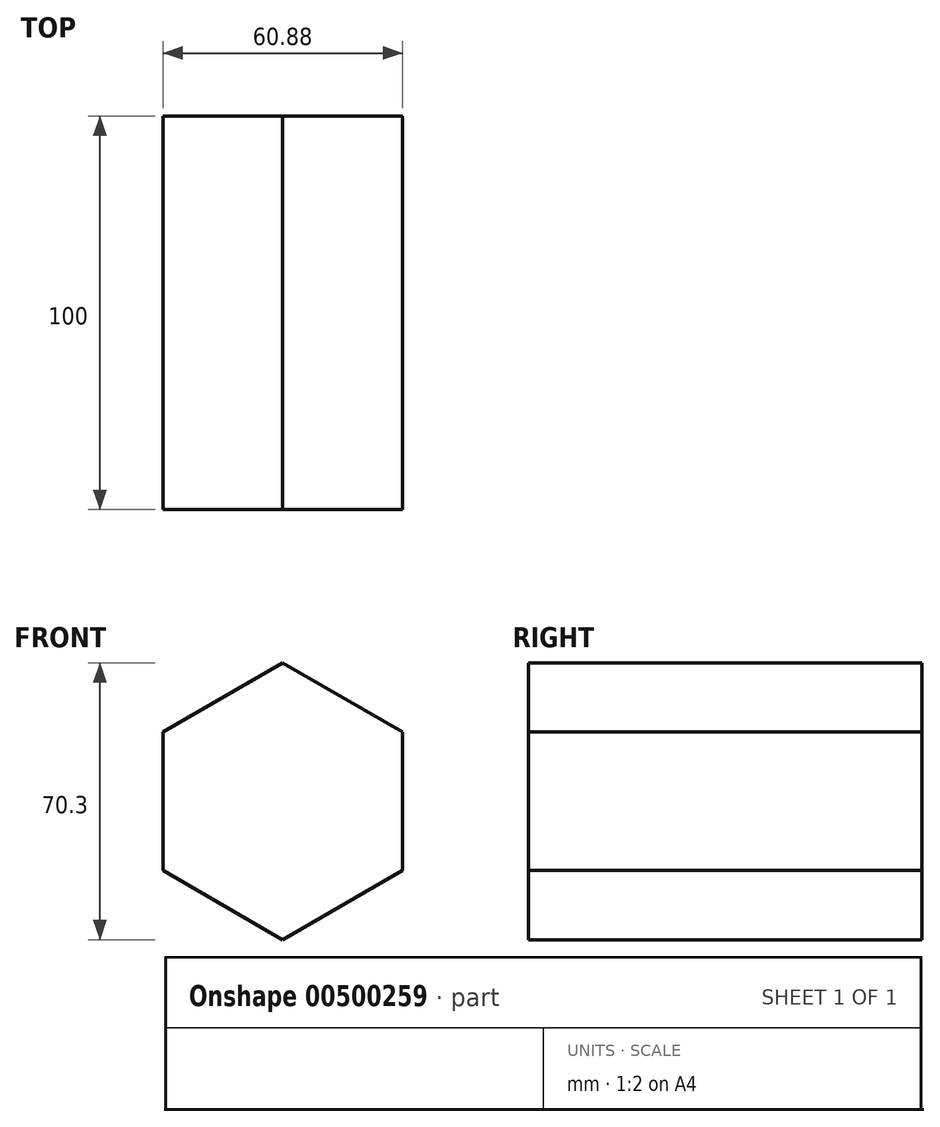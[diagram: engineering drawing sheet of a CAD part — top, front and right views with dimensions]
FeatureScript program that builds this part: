
annotation { "Feature Type Name" : "Feature", "Feature Type Description" : "" }
export const myFeature = defineFeature(function(context is Context, id is Id, definition is map)
    precondition{}
    {
        {
            var Q0;
            Q0=qCreatedBy(makeId("Front.planeOp"),FACE);
            var sketch = newSketch(context, id + "F0", { "sketchPlane" : qUnion([Q0])});
            skCircle(sketch, "E0.cCircle", {"center": v(0, 0) * mm, "radius": 35.15 * mm, "construction": true});
            skLineSegment(sketch, "E0.0", {"start": v(0, -35.15) * mm, "end": v(-30.44, -17.57) * mm});
            skLineSegment(sketch, "E0.1", {"start": v(-30.44, -17.57) * mm, "end": v(-30.44, 17.57) * mm});
            skLineSegment(sketch, "E0.2", {"start": v(-30.44, 17.57) * mm, "end": v(0, 35.15) * mm});
            skLineSegment(sketch, "E0.3", {"start": v(0, 35.15) * mm, "end": v(30.44, 17.57) * mm});
            skLineSegment(sketch, "E0.4", {"start": v(30.44, 17.57) * mm, "end": v(30.44, -17.57) * mm});
            skLineSegment(sketch, "E0.5", {"start": v(30.44, -17.57) * mm, "end": v(0, -35.15) * mm});
            skSolve(sketch);
        }
        {
            var Q0;
            Q0=makeQuery(id+"F0.imprint","IMPRINT",FACE,{"disambiguationData":[TD([[makeQuery(id+"F0.imprint","IMPRINT",EDGE,{"derivedFrom":sQuery(id+"F0.wireOp",EDGE,"E0.0")}),-1.0]])]});
            extrude(context, id + "F1", {"entities" : qUnion([Q0]), "depth" : 100 * mm});
        }
    });
